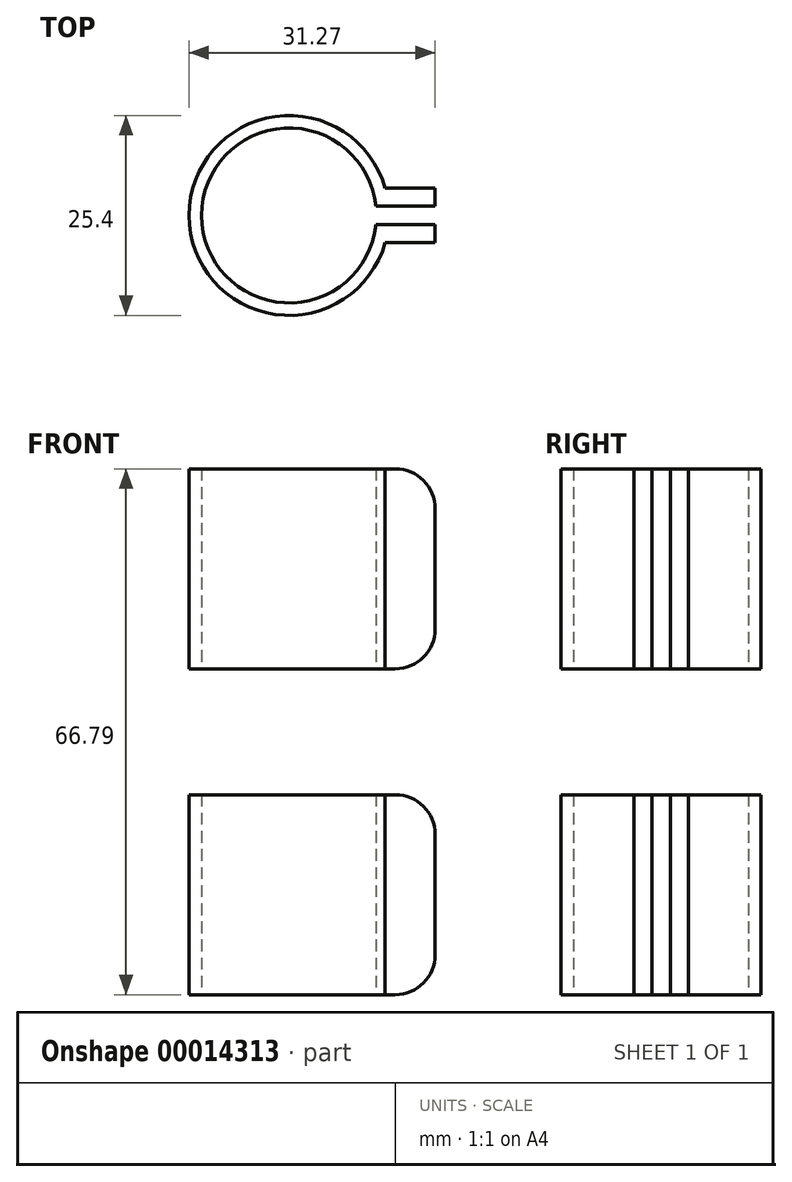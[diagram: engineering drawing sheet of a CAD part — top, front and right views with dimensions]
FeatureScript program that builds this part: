
annotation { "Feature Type Name" : "Feature", "Feature Type Description" : "" }
export const myFeature = defineFeature(function(context is Context, id is Id, definition is map)
    precondition{}
    {
        {
            var Q0;
            Q0=qCreatedBy(makeId("Top.planeOp"),FACE);
            var sketch = newSketch(context, id + "F0", { "sketchPlane" : qUnion([Q0])});
            skCircle(sketch, "E0", {"center": v(0, 0) * mm, "radius": 11.11 * mm});
            skCircle(sketch, "E1", {"center": v(0, 0) * mm, "radius": 12.7 * mm});
            skPoint(sketch, "E2.rect.middle", {"position": v(11.11, 0) * mm});
            skLineSegment(sketch, "E3", {"start": v(12.22, -3.47) * mm, "end": v(18.57, -3.47) * mm});
            skLineSegment(sketch, "E4", {"start": v(18.57, -1.17) * mm, "end": v(11.05, -1.17) * mm});
            skLineSegment(sketch, "E5", {"start": v(11.05, 1.17) * mm, "end": v(18.57, 1.17) * mm});
            skLineSegment(sketch, "E6", {"start": v(18.57, 3.47) * mm, "end": v(18.57, 1.17) * mm});
            skLineSegment(sketch, "E7", {"start": v(18.57, -1.17) * mm, "end": v(18.57, -3.47) * mm});
            skLineSegment(sketch, "E8", {"start": v(18.57, 3.47) * mm, "end": v(12.22, 3.47) * mm});
            skSolve(sketch);
        }
        {
            var Q0;
            {var subQ3=sQuery(id+"F0.wireOp",EDGE,"E0");var subQ5=sQuery(id+"F0.wireOp",EDGE,"E4");var subQ7=makeQuery(id+"F0.imprint","INTERSECT",VERTEX,{"derivedFrom":[subQ3,subQ5]});Q0=makeQuery(id+"F0.imprint","IMPRINT",FACE,{"disambiguationData":[TD([[makeQuery(id+"F0.imprint","IMPRINT",EDGE,{"disambiguationData":[TD([[subQ7,1.0]])],"derivedFrom":subQ3}),-1.0]])]});}
            var Q1;
            {var subQ1=sQuery(id+"F0.wireOp",EDGE,"E6");Q1=makeQuery(id+"F0.imprint","IMPRINT",FACE,{"disambiguationData":[TD([[makeQuery(id+"F0.imprint","IMPRINT",EDGE,{"derivedFrom":subQ1}),-1.0]])]});}
            var Q2;
            {var subQ4=sQuery(id+"F0.wireOp",EDGE,"E3");Q2=makeQuery(id+"F0.imprint","IMPRINT",FACE,{"disambiguationData":[TD([[makeQuery(id+"F0.imprint","IMPRINT",EDGE,{"derivedFrom":subQ4}),1.0]])]});}
            extrude(context, id + "F1", {"entities" : qUnion([Q0, Q1, Q2]), "depth" : 25.4 * mm});
        }
        {
            var Q0;
            Q0=makeQuery(id+"F1.opExtrude","CAP_EDGE",EDGE,{"disambiguationData":[OSD([sQuery(id+"F0.wireOp",EDGE,"E7")])],"isStart":false});
            var Q1;
            Q1=makeQuery(id+"F1.opExtrude","CAP_EDGE",EDGE,{"disambiguationData":[OSD([sQuery(id+"F0.wireOp",EDGE,"E6")])],"isStart":false});
            var Q2;
            Q2=makeQuery(id+"F1.opExtrude","CAP_EDGE",EDGE,{"disambiguationData":[OSD([sQuery(id+"F0.wireOp",EDGE,"E7")])],"isStart":true});
            var Q3;
            Q3=makeQuery(id+"F1.opExtrude","CAP_EDGE",EDGE,{"disambiguationData":[OSD([sQuery(id+"F0.wireOp",EDGE,"E6")])],"isStart":true});
            fillet(context, id + "F2", {"entities" : qUnion([Q0, Q1, Q2, Q3]), "radius" : 5.08 * mm, "tangentPropagation" : true, "allowEdgeOverflow" : false});
        }
        {
            var Q0;
            Q0=makeQuery(id+"F1.opExtrude","SWEPT_BODY",BODY,{"disambiguationData":[OSD([sQuery(id+"F0.wireOp",EDGE,"E0"),sQuery(id+"F0.wireOp",EDGE,"E1"),sQuery(id+"F0.wireOp",EDGE,"E3"),sQuery(id+"F0.wireOp",EDGE,"E4"),sQuery(id+"F0.wireOp",EDGE,"E5"),sQuery(id+"F0.wireOp",EDGE,"E6"),sQuery(id+"F0.wireOp",EDGE,"E7"),sQuery(id+"F0.wireOp",EDGE,"E8")])]});
            transform(context, id + "F3", {"entities" : qUnion([Q0]), "transformType" : TransformType.TRANSLATION_3D, "dx" : 0 * mm, "dy" : 0 * mm, "dz" : 0 * mm, "makeCopy" : true});
        }
        {
            var Q0;
            Q0=makeQuery(id+"F3.opPattern","COPY",BODY,{"derivedFrom":makeQuery(id+"F1.opExtrude","SWEPT_BODY",BODY,{"disambiguationData":[OSD([sQuery(id+"F0.wireOp",EDGE,"E0"),sQuery(id+"F0.wireOp",EDGE,"E1"),sQuery(id+"F0.wireOp",EDGE,"E3"),sQuery(id+"F0.wireOp",EDGE,"E4"),sQuery(id+"F0.wireOp",EDGE,"E5"),sQuery(id+"F0.wireOp",EDGE,"E6"),sQuery(id+"F0.wireOp",EDGE,"E7"),sQuery(id+"F0.wireOp",EDGE,"E8")])]}),"instanceName":"1"});
            transform(context, id + "F4", {"entities" : qUnion([Q0]), "transformType" : TransformType.TRANSLATION_3D, "dx" : 0 * mm, "dy" : 0 * mm, "dz" : 41.4 * mm, "makeCopy" : true});
        }
        {
            var Q0;
            Q0=makeQuery(id+"F3.opPattern","COPY",BODY,{"derivedFrom":makeQuery(id+"F1.opExtrude","SWEPT_BODY",BODY,{"disambiguationData":[OSD([sQuery(id+"F0.wireOp",EDGE,"E0"),sQuery(id+"F0.wireOp",EDGE,"E1"),sQuery(id+"F0.wireOp",EDGE,"E3"),sQuery(id+"F0.wireOp",EDGE,"E4"),sQuery(id+"F0.wireOp",EDGE,"E5"),sQuery(id+"F0.wireOp",EDGE,"E6"),sQuery(id+"F0.wireOp",EDGE,"E7"),sQuery(id+"F0.wireOp",EDGE,"E8")])]}),"instanceName":"1"});
            deleteBodies(context, id + "F5", {"entities" : qUnion([Q0])});
        }
    });
